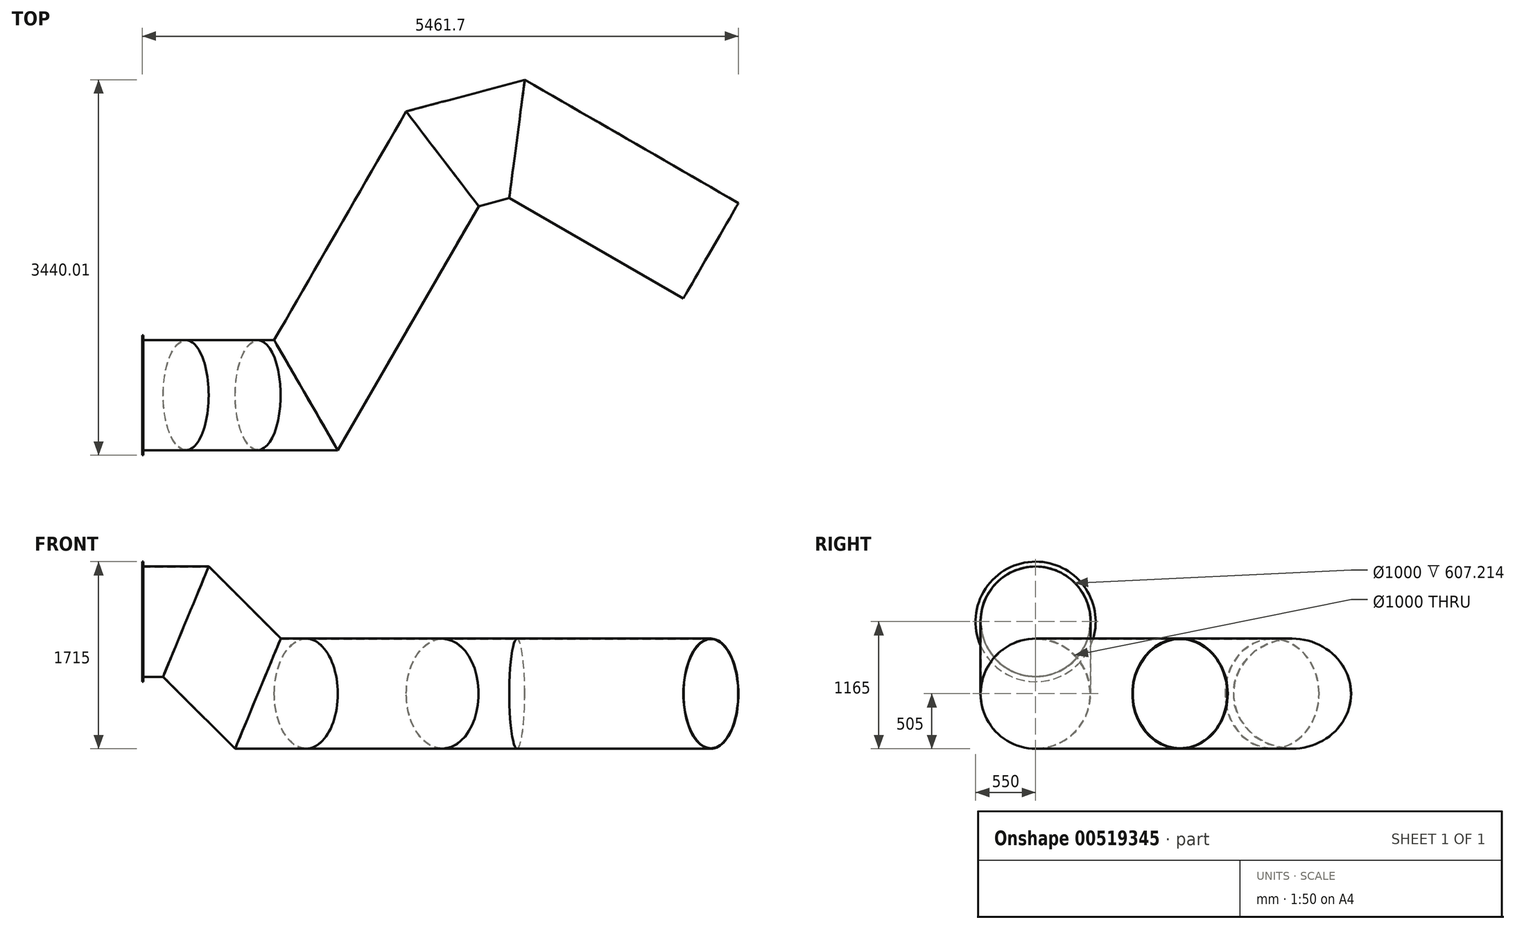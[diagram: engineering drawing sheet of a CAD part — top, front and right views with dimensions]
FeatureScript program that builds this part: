
annotation { "Feature Type Name" : "Feature", "Feature Type Description" : "" }
export const myFeature = defineFeature(function(context is Context, id is Id, definition is map)
    precondition{}
    {
        {
            var Q0;
            Q0=qCreatedBy(makeId("Front.planeOp"),FACE);
            var sketch = newSketch(context, id + "F0", { "sketchPlane" : qUnion([Q0])});
            skLineSegment(sketch, "E0", {"start": v(0, 0) * mm, "end": v(400, 0) * mm});
            skLineSegment(sketch, "E1", {"start": v(400, 0) * mm, "end": v(1060, -660) * mm});
            skLineSegment(sketch, "E2", {"start": v(1060, -660) * mm, "end": v(1500, -660) * mm});
            skSolve(sketch);
        }
        {
            var Q0;
            Q0=qCreatedBy(makeId("Top.planeOp"),FACE);
            cPlane(context, id + "F1", {"entities" : qUnion([Q0]), "cplaneType" : CPlaneType.OFFSET, "offset" : 660 * mm, "oppositeDirection" : true, "width" : 150 * mm, "height" : 150 * mm});
        }
        {
            var Q0;
            Q0=qCreatedBy(id+"F1.planeOp",FACE);
            var sketch = newSketch(context, id + "F2", { "sketchPlane" : qUnion([Q0])});
            skPoint(sketch, "E3.0", {"position": v(1500, 0) * mm});
            skLineSegment(sketch, "E4", {"start": v(1500, 0) * mm, "end": v(2750, 2165.06) * mm});
            skLineSegment(sketch, "E5", {"start": v(3433.01, 2348.08) * mm, "end": v(5209.2, 1322.6) * mm});
            skLineSegment(sketch, "E6", {"start": v(5209.2, 1322.6) * mm, "end": v(4959.2, 889.58) * mm, "construction": true});
            skLineSegment(sketch, "E7", {"start": v(2750, 2165.06) * mm, "end": v(3433.01, 2348.08) * mm});
            skPoint(sketch, "E8.0", {"position": v(0, 0) * mm});
            skSolve(sketch);
        }
        {
            var Q0;
            Q0=qCreatedBy(makeId("Right.planeOp"),FACE);
            var sketch = newSketch(context, id + "F3", { "sketchPlane" : qUnion([Q0])});
            skCircle(sketch, "E9", {"center": v(0, 0) * mm, "radius": 500 * mm});
            skCircle(sketch, "E10", {"center": v(0, 0) * mm, "radius": 505 * mm});
            skSolve(sketch);
        }
        {
            var Q0;
            Q0 = qSketchRegion(id + "F3", true);
            var Q1;
            Q1 = qConstructionFilter(qBodyType(qCreatedBy(id + "F0" ,EDGE), BodyType.WIRE), ConstructionObject.NO);
            var Q2;
            Q2 = qConstructionFilter(qBodyType(qCreatedBy(id + "F2" ,EDGE), BodyType.WIRE), ConstructionObject.NO);
            sweep(context, id + "F4", {"profiles" : qUnion([Q0]), "path" : qUnion([Q1, Q2])});
        }
        {
            var Q0;
            Q0=makeQuery(id+"F4.opSweep","CAP_FACE",FACE,{"disambiguationData":[OSD([sQuery(id+"F0.wireOp",VERTEX,"E0.start"),sQuery(id+"F3.wireOp",EDGE,"E9"),sQuery(id+"F3.wireOp",EDGE,"E10")])],"isStart":true});
            var sketch = newSketch(context, id + "F5", { "sketchPlane" : qUnion([Q0])});
            skCircle(sketch, "E11.0", {"center": v(0, 0) * mm, "radius": 500 * mm});
            skCircle(sketch, "E12", {"center": v(0, 0) * mm, "radius": 550 * mm});
            skSolve(sketch);
        }
        {
            var Q0;
            Q0 = qSketchRegion(id + "F5", true);
            extrude(context, id + "F6", {"entities" : qUnion([Q0]), "operationType" : NewBodyOperationType.ADD, "oppositeDirection" : true, "depth" : 10 * mm, "offsetDistance" : 25 * mm});
        }
    });
